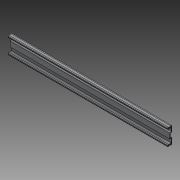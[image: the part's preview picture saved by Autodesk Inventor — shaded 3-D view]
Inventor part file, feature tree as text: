
AUTODESK INVENTOR PART (.ipt)
format: ipt  version: 2014 SP1 (Build 180222100, 222)  size: 195,072 bytes
history: native  units: in
note: dims shown in document units (in); Inventor stores cm internally (conversion verified against a paired STEP export)
features: extrude x1, other x1, imported_body x1
ambient origin geometry x8: Origin, YZ Plane, XZ Plane, XY Plane, X Axis, Y Axis, Z Axis, Center Point
bodies: Body1 (feature_tree)
feature tree (3):
  extrude  "Extrude3"  [1 undecoded]
  other  "63835A4201"
  imported_body  "Base1"
note: 1 required parameter value undecoded (feature->parameter linkage not recoverable at this tier; creation-order binding heuristic only, values carry confidence <= 0.55)
